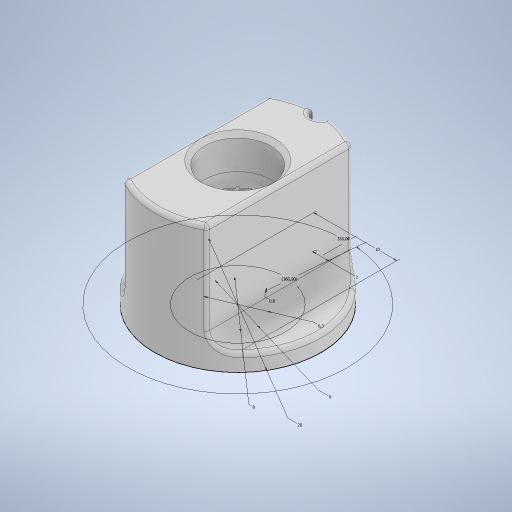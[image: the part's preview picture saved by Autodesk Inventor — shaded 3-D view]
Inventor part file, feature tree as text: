
AUTODESK INVENTOR PART (.ipt)
format: ipt  version: 2024 (Build 280153000, 153)  size: 598,016 bytes
history: native  units: mm
features: extrude x7, fillet x6, sketch x3, other x1, revolve x1, chamfer x1, projected_geometry x1
ambient origin geometry x8: Origin, YZ Plane, XZ Plane, XY Plane, X Axis, Y Axis, Z Axis, Center Point
bodies: Body1 (feature_tree)
feature tree (20):
  other  "Твердое тело1"
  sketch  "Эскиз1"
  extrude  "Выдавливание1"  Depth=6.15mm
  extrude  "Выдавливание2"  Depth=8.0mm
  extrude  "Выдавливание3"  Depth=0.8mm
  extrude  "Выдавливание4"  Depth=180.0mm TaperAngle=360.0deg
  extrude  "Выдавливание5"  Depth=20.0mm
  fillet  "Сопряжение2"  Radius=10.0mm
  revolve  "Вращение1"
  fillet  "Сопряжение3"  Radius=8.0mm
  chamfer  "Фаска1"  Distance=2.0mm
  fillet  "Сопряжение7"  Radius=2.0mm
  fillet  "Сопряжение8"  Radius=15.0mm
  extrude  "Выдавливание7"  Depth=4.0mm TaperAngle=0.0deg
  extrude  "Выдавливание8"  TaperAngle=0.0deg  [1 undecoded]
  fillet  "Сопряжение12"  Radius=5.0mm
  fillet  "Сопряжение13"  Radius=1.0mm
  sketch  "Эскиз2"
  projected_geometry  "Спроецированная петля1"
  sketch  "Эскиз4"
note: 1 required parameter value undecoded (feature->parameter linkage not recoverable at this tier; creation-order binding heuristic only, values carry confidence <= 0.55)
